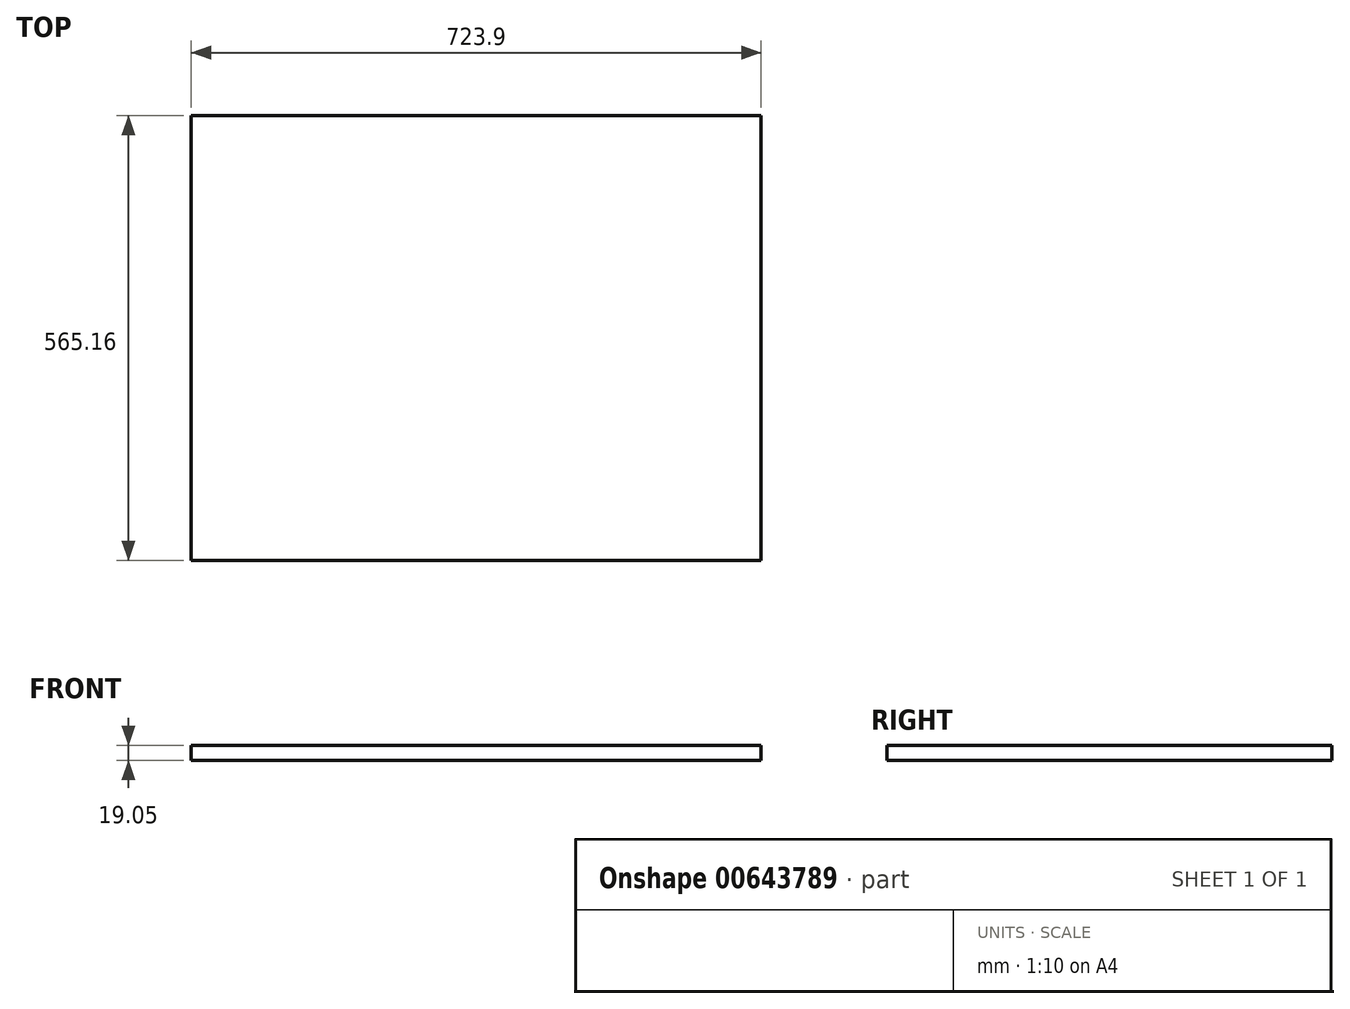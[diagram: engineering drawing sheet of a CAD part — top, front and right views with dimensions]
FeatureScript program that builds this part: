
annotation { "Feature Type Name" : "Feature", "Feature Type Description" : "" }
export const myFeature = defineFeature(function(context is Context, id is Id, definition is map)
    precondition{}
    {
        {
            var Q0;
            Q0=qCreatedBy(makeId("Top.planeOp"),FACE);
            var sketch = newSketch(context, id + "F0", { "sketchPlane" : qUnion([Q0])});
            skLineSegment(sketch, "E0.bottom", {"start": v(-361.95, 282.58) * mm, "end": v(361.95, 282.58) * mm});
            skLineSegment(sketch, "E0.top", {"start": v(-361.95, -282.58) * mm, "end": v(361.95, -282.58) * mm});
            skLineSegment(sketch, "E0.left", {"start": v(-361.95, 282.58) * mm, "end": v(-361.95, -282.58) * mm});
            skLineSegment(sketch, "E0.right", {"start": v(361.95, 282.58) * mm, "end": v(361.95, -282.58) * mm});
            skPoint(sketch, "E0.middle", {"position": v(0, 0) * mm});
            skSolve(sketch);
        }
        {
            var Q0;
            Q0=makeQuery(id+"F0.imprint","IMPRINT",FACE,{"disambiguationData":[TD([[makeQuery(id+"F0.imprint","IMPRINT",EDGE,{"derivedFrom":sQuery(id+"F0.wireOp",EDGE,"E0.bottom")}),-1.0]])]});
            extrude(context, id + "F1", {"entities" : qUnion([Q0]), "depth" : 19.05 * mm, "offsetDistance" : 25.4 * mm});
        }
    });
